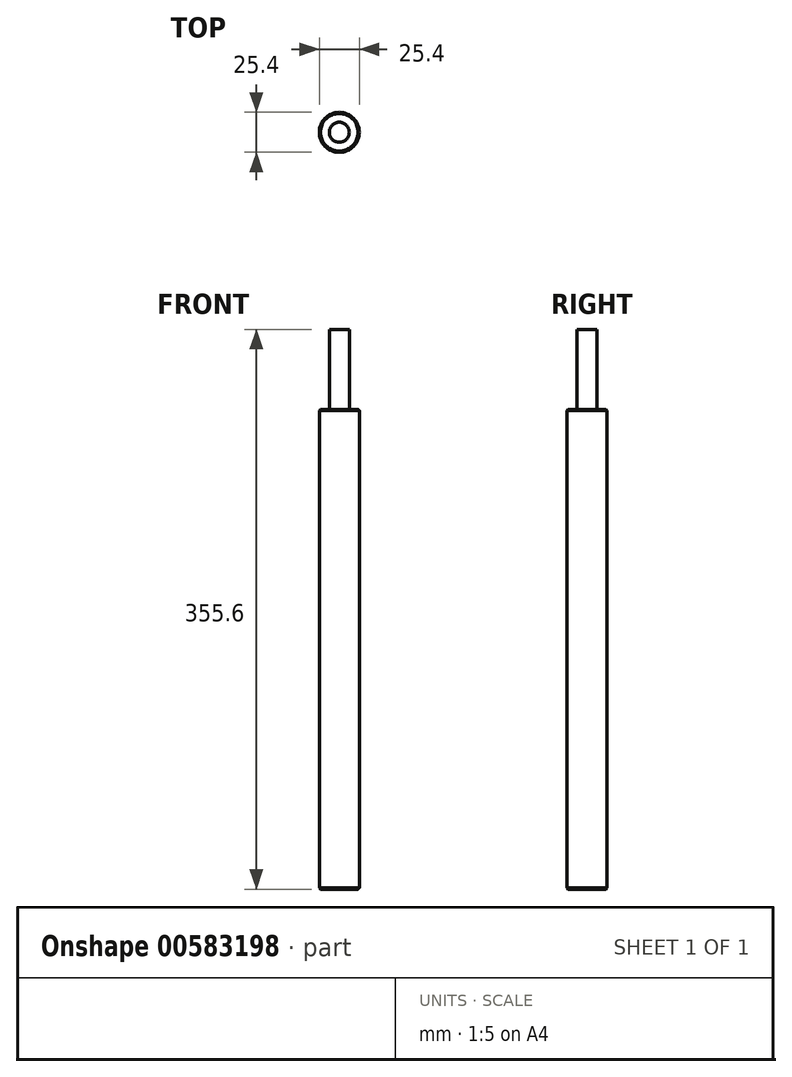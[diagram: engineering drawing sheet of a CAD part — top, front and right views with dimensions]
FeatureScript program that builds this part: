
annotation { "Feature Type Name" : "Feature", "Feature Type Description" : "" }
export const myFeature = defineFeature(function(context is Context, id is Id, definition is map)
    precondition{}
    {
        {
            var Q0;
            Q0=qCreatedBy(makeId("Top.planeOp"),FACE);
            var sketch = newSketch(context, id + "F0", { "sketchPlane" : qUnion([Q0])});
            skCircle(sketch, "E0", {"center": v(0, 0) * mm, "radius": 12.7 * mm});
            skSolve(sketch);
        }
        {
            var Q0;
            Q0 = qSketchRegion(id + "F0", true);
            extrude(context, id + "F1", {"entities" : qUnion([Q0]), "depth" : 304.8 * mm, "offsetDistance" : 25.4 * mm});
        }
        {
            var Q0;
            Q0=makeQuery(id+"F1.opExtrude","CAP_EDGE",EDGE,{"disambiguationData":[OSD([sQuery(id+"F0.wireOp",EDGE,"E0")])],"isStart":true});
            var Q1;
            Q1=makeQuery(id+"F1.opExtrude","CAP_EDGE",EDGE,{"disambiguationData":[OSD([sQuery(id+"F0.wireOp",EDGE,"E0")])],"isStart":false});
            chamfer(context, id + "F2", {"entities" : qUnion([Q0, Q1]), "width" : 0.76 * mm, "tangentPropagation" : true});
        }
        {
            var Q0;
            Q0=makeQuery(id+"F1.opExtrude","CAP_FACE",FACE,{"disambiguationData":[OSD([sQuery(id+"F0.wireOp",EDGE,"E0")])],"isStart":false});
            var sketch = newSketch(context, id + "F3", { "sketchPlane" : qUnion([Q0])});
            skCircle(sketch, "E1", {"center": v(0, 0) * mm, "radius": 6.35 * mm});
            skSolve(sketch);
        }
        {
            var Q0;
            Q0 = qSketchRegion(id + "F3", true);
            extrude(context, id + "F4", {"entities" : qUnion([Q0]), "operationType" : NewBodyOperationType.ADD, "depth" : 50.8 * mm, "offsetDistance" : 25.4 * mm});
        }
    });
